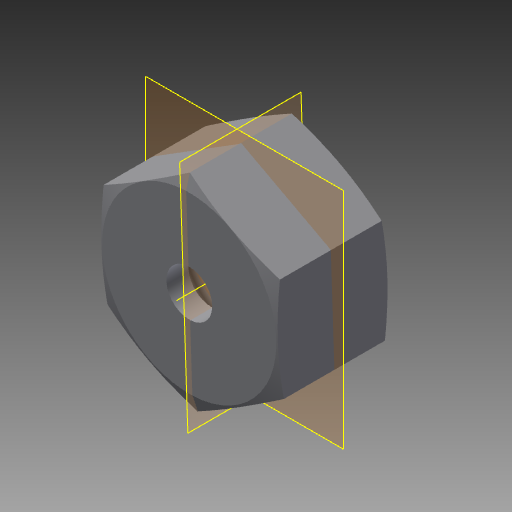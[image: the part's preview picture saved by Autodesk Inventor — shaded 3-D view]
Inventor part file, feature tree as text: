
AUTODESK INVENTOR PART (.ipt)
format: ipt  version: 2017.1 (Build 211199000, 199)  size: 146,432 bytes
history: native  units: in
note: dims shown in document units (in); Inventor stores cm internally (conversion verified against a paired STEP export)
features: sketch x4, plane x3, extrude x3, reference x2, thread x1, other x1, revolve x1, mirror x1
ambient origin geometry x8: Origin, YZ Plane, XZ Plane, XY Plane, X Axis, Y Axis, Z Axis, Center Point
bodies: Body1 (feature_tree)
feature tree (16):
  plane  "Work Plane3"
  extrude  "Extrusion2"  Depth=0.5in
  extrude  "Extrusion3"  Depth=0.375in TaperAngle=0.0deg
  extrude  "Extrusion4"  TaperAngle=90.0deg  [1 undecoded]
  thread  "Thread1"  [1 undecoded]
  plane  "Work Plane4"
  other  "Work Axis4"
  revolve  "Revolution2"  [1 undecoded]
  plane  "Work Plane5"
  mirror  "Mirror1"
  sketch  "Sketch6"  dims[d3=0.3125in d4=0.0in d5=0.5in]
  sketch  "Sketch7"  dims[d6=0.25in d7=-0.0123in d8=0.375in d9=0.0in]
  reference  "Reference1"
  sketch  "Sketch8"  dims[d10=0.392in d11=0.0in d12=90.0deg d13=0.045in]
  reference  "Reference2"
  sketch  "Sketch9"
note: 3 required parameter values undecoded (feature->parameter linkage not recoverable at this tier; creation-order binding heuristic only, values carry confidence <= 0.55)
